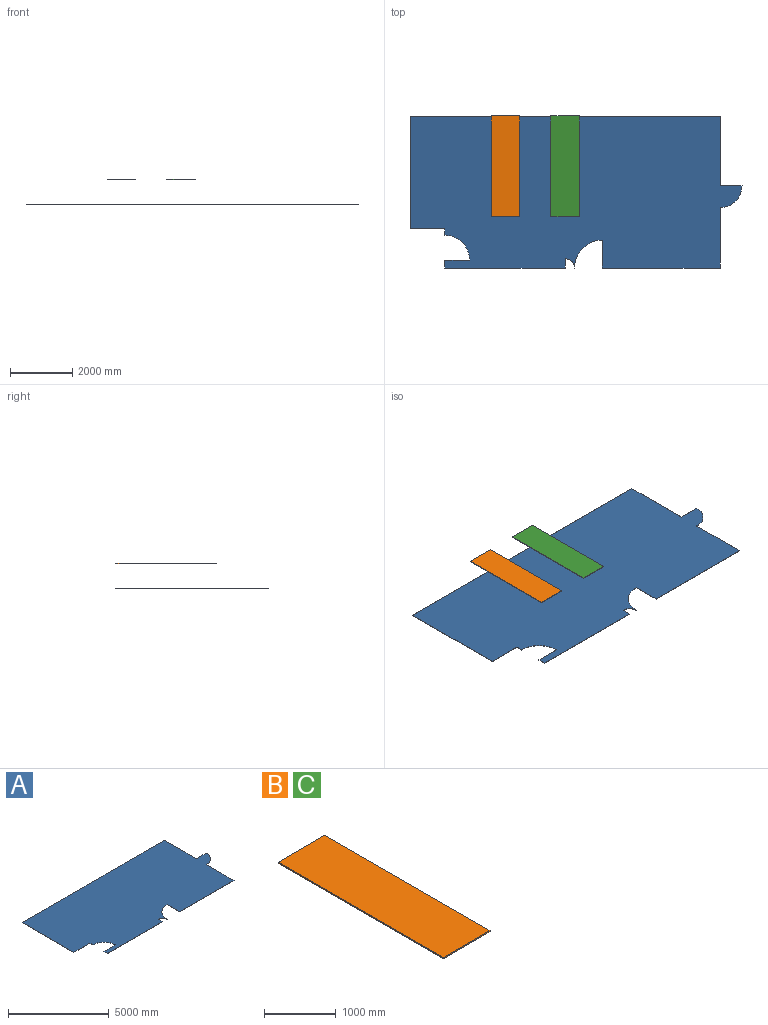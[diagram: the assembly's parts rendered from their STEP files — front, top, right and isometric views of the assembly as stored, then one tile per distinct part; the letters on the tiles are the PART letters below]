
ASSEMBLY  parts=3 mates=3
PART A: 19 faces, bbox 10700x4900x10 mm
  f0: plane 10000x10mm, normal (0,1,0), area 100000mm2, adj f1,f16,f17,f18
  f1: plane 3640x10mm, normal (-1,0,0), area 36400mm2, adj f0,f2,f17,f18
  f2: plane 1120x10mm, normal (0,-1,0), area 11200mm2, adj f1,f3,f17,f18
  f3: plane 202.19x10mm, normal (-1,0,0), area 2021.9mm2, adj f2,f4,f17,f18
  f4: cylinder r=800mm len=800mm, axis (0,0,1), area 12566.4mm2, adj f3,f5,f17,f18
  f5: plane 800x10mm, normal (0,1,0), area 8000mm2, adj f4,f6,f17,f18
  f6: plane 257.81x10mm, normal (-1,0,0), area 2578.1mm2, adj f5,f7,f17,f18
  f7: plane 3880x10mm, normal (0,-1,0), area 38800mm2, adj f6,f8,f17,f18
  f8: plane 300x10mm, normal (1,0,0), area 3000mm2, adj f7,f9,f17,f18
  f9: cylinder r=300mm len=300mm, axis (0,0,1), area 4712.4mm2, adj f8,f10,f17,f18
  f10: cylinder r=900mm len=900mm, axis (0,0,1), area 14137.2mm2, adj f9,f11,f17,f18
  f11: plane 900x10mm, normal (-1,0,0), area 9000mm2, adj f10,f12,f17,f18
  f12: plane 3800x10mm, normal (0,-1,0), area 38000mm2, adj f11,f13,f17,f18
  f13: plane 1950x10mm, normal (1,0,0), area 19500mm2, adj f12,f14,f17,f18
  f14: cylinder r=700mm len=700mm, axis (0,0,1), area 10995.6mm2, adj f13,f15,f17,f18
  f15: plane 700x10mm, normal (0,1,0), area 7000mm2, adj f14,f16,f17,f18
  f16: plane 2250x10mm, normal (1,0,0), area 22500mm2, adj f0,f15,f17,f18
  f17: plane 10700x4900mm, normal (0,0,-1), area 46764131.9mm2, adj f0,f1,f2,f3,f4,f5,f6,f7
  f18: plane 10700x4900mm, normal (0,0,1), area 46764131.9mm2, adj f0,f1,f2,f3,f4,f5,f6,f7
PART B: 6 faces, bbox 920x3250x20 mm
  f0: plane 920x20mm, normal (0,1,0), area 18400mm2, adj f1,f3,f4,f5
  f1: plane 3250x20mm, normal (-1,0,0), area 65000mm2, adj f0,f2,f4,f5
  f2: plane 920x20mm, normal (0,-1,0), area 18400mm2, adj f1,f3,f4,f5
  f3: plane 3250x20mm, normal (1,0,0), area 65000mm2, adj f0,f2,f4,f5
  f4: plane 3250x920mm, normal (0,0,1), area 2990000mm2, adj f0,f1,f2,f3
  f5: plane 3250x920mm, normal (0,0,-1), area 2990000mm2, adj f0,f1,f2,f3
PART C: same geometry as B
PLACE A t=(-5964.34,-3094.9,817.01)mm
PLACE B t=(-1129.56,-2419.65,1622.01)mm
PLACE C t=(790.44,-2419.65,1622.01)mm
MATE parallel C.f5 <-> A.f18  axis (0,0,-1) through (-136.68,105.68,1622.01)mm
MATE parallel B.f3 <-> C.f1  axis (1,0,0) through (-1596.68,105.68,1632.01)mm
MATE parallel A.f0 <-> C.f0  axis (0,1,0) through (-136.68,1730.68,812.01)mm
